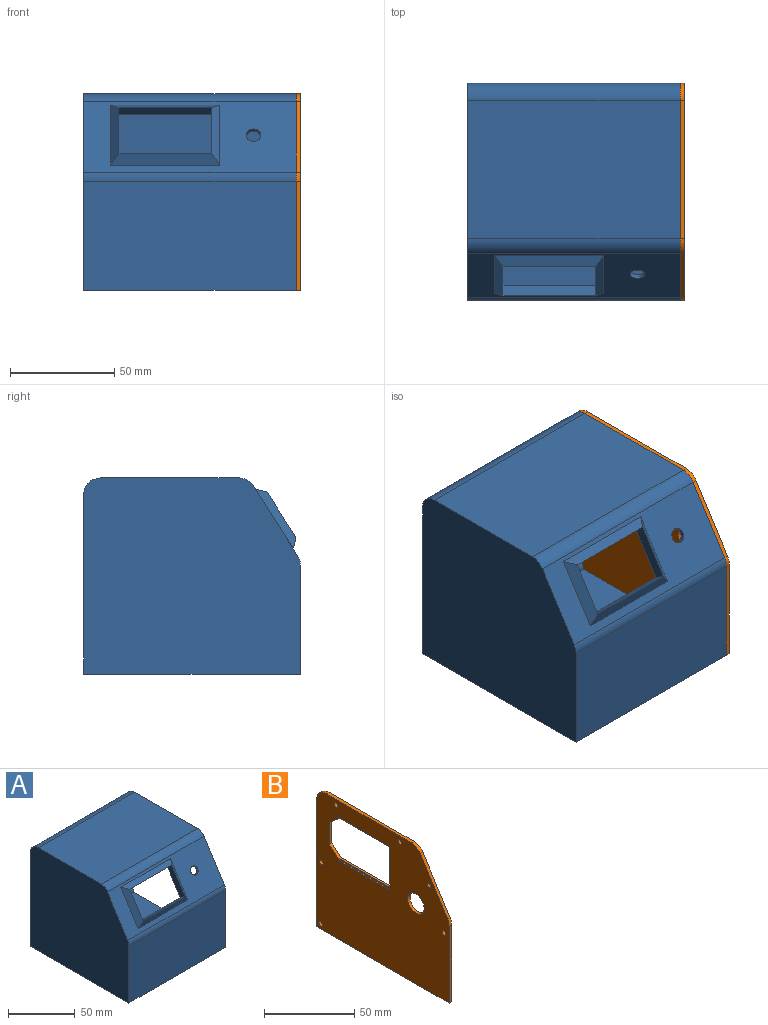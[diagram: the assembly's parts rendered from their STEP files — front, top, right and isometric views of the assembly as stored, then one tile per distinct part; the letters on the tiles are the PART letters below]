
ASSEMBLY  parts=2 mates=1
PART A: 61 faces, bbox 102x104x94 mm
  f0: plane 102x33.74mm, normal (0,-0.84,0.54), area 2255.6mm2, adj f6,f8,f13,f21,f22,f57,f58,f59
  f1: plane 100x49.68mm, normal (0,1,0), area 4888mm2, adj f2,f6,f12,f19,f34,f35,f41,f54
  f2: plane 100x100mm, normal (0,0,1), area 9959.9mm2, adj f1,f6,f11,f12,f32,f33,f38,f54
  f3: plane 100x63.5mm, normal (0,0,-1), area 6204.9mm2, adj f6,f12,f18,f20,f26,f27,f28,f29
  f4: plane 100x32.32mm, normal (0,0.84,-0.54), area 2562.5mm2, adj f6,f12,f13,f14,f15,f16,f17,f19
  f5: plane 102x52.26mm, normal (0,-1,0), area 5330.3mm2, adj f6,f8,f10,f22
  f6: plane 104x94mm, normal (1,0,0), area 931mm2, adj f0,f1,f2,f3,f4,f5,f7,f9
  f7: plane 102x86mm, normal (0,1,0), area 8772mm2, adj f6,f8,f10,f23
  f8: plane 104x94mm, normal (-1,0,0), area 9265.9mm2, adj f0,f5,f7,f9,f10,f21,f22,f23
  f9: plane 102x66.6mm, normal (0,0,1), area 6792.9mm2, adj f6,f8,f21,f23
  f10: plane 104x102mm, normal (0,0,-1), area 10608mm2, adj f5,f6,f7,f8
  f11: plane 100x82mm, normal (0,-1,0), area 8094.8mm2, adj f2,f6,f12,f18,f30,f31,f32,f33
  f12: plane 100x90mm, normal (1,0,0), area 8524.8mm2, adj f1,f2,f3,f4,f11,f18,f19,f20
  f13: cylinder r=3.5mm len=7mm, axis (0,-0.84,0.54), area 44mm2, adj f0,f4
  f14: plane 44.4x5.07mm, normal (0,-0.54,-0.84), area 266.4mm2, adj f4,f15,f17,f58
  f15: plane 25.17x18.99mm, normal (1,0,0), area 156mm2, adj f4,f14,f16,f59
  f16: plane 44.4x5.07mm, normal (0,0.54,0.84), area 266.4mm2, adj f4,f15,f17,f60
  f17: plane 25.17x18.99mm, normal (-1,0,0), area 156mm2, adj f4,f14,f16,f57
  f18: cylinder r=8mm len=100mm, axis (-1,0,0), area 1256.6mm2, adj f3,f6,f11,f12,f28
  f19: cylinder r=8mm len=100mm, axis (-1,0,0), area 452.2mm2, adj f1,f4,f6,f12
  f20: cylinder r=8mm len=100mm, axis (-1,0,0), area 804.4mm2, adj f3,f4,f6,f12
  f21: cylinder r=8mm len=102mm, axis (1,0,0), area 820.5mm2, adj f0,f6,f8,f9
  f22: cylinder r=8mm len=102mm, axis (1,0,0), area 461.3mm2, adj f0,f5,f6,f8
  f23: cylinder r=8mm len=102mm, axis (1,0,0), area 1281.8mm2, adj f6,f7,f8,f9
  f24: cylinder r=5.5mm len=10.14mm, axis (1,0,0), area 86.4mm2, adj f4,f6,f40
  f25: plane 0.56x0.47mm, normal (-1,0,0), area 0.1mm2, adj f4,f40
  f26: cylinder r=5.5mm len=11mm, axis (1,0,0), area 86.4mm2, adj f3,f6,f39
  f27: plane 0.61x0.3mm, normal (-1,0,0), area 0.1mm2, adj f3,f39
  f28: cylinder r=5.5mm len=11mm, axis (1,0,0), area 86.4mm2, adj f3,f6,f18,f36
  f29: plane 0.61x0.3mm, normal (-1,0,0), area 0.1mm2, adj f3,f36
  f30: cylinder r=5.5mm len=11mm, axis (1,0,0), area 86.4mm2, adj f6,f11,f37
  f31: plane 0.61x0.3mm, normal (-1,0,0), area 0.1mm2, adj f11,f37
  f32: cylinder r=5mm len=5mm, axis (1,0,0), area 39.3mm2, adj f2,f6,f11,f38
  f33: plane 0.2x0.2mm, normal (-1,0,0), area 0mm2, adj f2,f11,f38
  f34: cylinder r=5.5mm len=11mm, axis (1,0,0), area 86.4mm2, adj f1,f6,f41
  f35: plane 0.61x0.3mm, normal (-1,0,0), area 0.1mm2, adj f1,f41
  f36: cone r=0.3mm half-angle=60deg, axis (1,0,0), area 54.7mm2, adj f3,f28,f29
  f37: cone r=0.3mm half-angle=60deg, axis (1,0,0), area 54.7mm2, adj f11,f30,f31
  f38: cone r=0.2mm half-angle=58deg, axis (1,0,0), area 23.1mm2, adj f2,f11,f32,f33
  f39: cone r=5.5mm half-angle=60deg, axis (1,0,0), area 54.7mm2, adj f3,f26,f27
  f40: cone r=5.5mm half-angle=60deg, axis (1,0,0), area 54.7mm2, adj f4,f24,f25
  f41: cone r=5.5mm half-angle=60deg, axis (1,0,0), area 54.7mm2, adj f1,f34,f35
  f42: cylinder r=2mm len=5mm, axis (1,0,0), area 62.8mm2, adj f6,f43
  f43: plane 4x4mm, normal (1,0,0), area 12.6mm2, adj f42
  f44: cylinder r=2mm len=5mm, axis (1,0,0), area 62.8mm2, adj f6,f45
  f45: plane 4x4mm, normal (1,0,0), area 12.6mm2, adj f44
  f46: cylinder r=2mm len=5mm, axis (1,0,0), area 62.8mm2, adj f6,f47
  f47: plane 4x4mm, normal (1,0,0), area 12.6mm2, adj f46
  f48: cylinder r=2mm len=5mm, axis (1,0,0), area 62.8mm2, adj f6,f49
  f49: plane 4x4mm, normal (1,0,0), area 12.6mm2, adj f48
  f50: cylinder r=2mm len=5mm, axis (1,0,0), area 62.8mm2, adj f6,f51
  f51: plane 4x4mm, normal (1,0,0), area 12.6mm2, adj f50
  f52: cylinder r=2mm len=5mm, axis (1,0,0), area 62.8mm2, adj f6,f53
  f53: plane 4x4mm, normal (1,0,0), area 12.6mm2, adj f52
  f54: plane 4x4mm, normal (0,0.71,0.71), area 5.7mm2, adj f1,f2,f6,f56
  f55: plane 2.59x2.59mm, normal (-1,0,0), area 3.3mm2, adj f1,f2,f56
  f56: plane 4x4mm, normal (-0.71,0.5,0.5), area 6.6mm2, adj f1,f2,f54,f55
  f57: plane 28.71x19.45mm, normal (0.71,-0.6,0.38), area 169.7mm2, adj f0,f17,f58,f60
  f58: plane 52.4x5.52mm, normal (0,-0.22,0.98), area 273.8mm2, adj f0,f14,f57,f59
  f59: plane 28.71x19.45mm, normal (-0.71,-0.6,0.38), area 169.7mm2, adj f0,f15,f58,f60
  f60: plane 52.4x5.52mm, normal (0,-0.98,-0.22), area 273.8mm2, adj f0,f16,f57,f59
PART B: 29 faces, bbox 2x104x94 mm
  f0: plane 104x94mm, normal (-1,0,0), area 7751.4mm2, adj f2,f3,f4,f5,f6,f7,f8,f9
  f1: plane 104x94mm, normal (1,0,0), area 7831.4mm2, adj f2,f3,f4,f5,f6,f7,f8,f9
  f2: cylinder r=8mm len=8mm, axis (-1,0,0), area 25.1mm2, adj f0,f1,f3,f9
  f3: plane 66.6x2mm, normal (0,0,1), area 133.2mm2, adj f0,f1,f2,f4
  f4: cylinder r=8mm len=6.76mm, axis (-1,0,0), area 16.1mm2, adj f0,f1,f3,f5
  f5: plane 33.74x21.4mm, normal (0,-0.84,0.54), area 79.9mm2, adj f0,f1,f4,f6
  f6: cylinder r=8mm len=4.29mm, axis (-1,0,0), area 9mm2, adj f0,f1,f5,f7
  f7: plane 52.26x2mm, normal (0,-1,0), area 104.5mm2, adj f0,f1,f6,f8
  f8: plane 104x2mm, normal (0,0,-1), area 208mm2, adj f0,f1,f7,f9
  f9: plane 86x2mm, normal (0,1,0), area 172mm2, adj f0,f1,f2,f8
  f10: cylinder r=1.5mm len=3mm, axis (1,0,0), area 18.8mm2, adj f0,f1
  f11: cylinder r=1.5mm len=3mm, axis (1,0,0), area 18.8mm2, adj f0,f1
  f12: cylinder r=1.5mm len=3mm, axis (1,0,0), area 18.8mm2, adj f0,f1
  f13: cylinder r=1.5mm len=3mm, axis (1,0,0), area 18.8mm2, adj f0,f1
  f14: cylinder r=1.5mm len=3mm, axis (1,0,0), area 18.8mm2, adj f0,f1
  f15: cylinder r=1.5mm len=3mm, axis (1,0,0), area 18.8mm2, adj f0,f1
  f16: plane 29.5x2mm, normal (0,1,0), area 56.6mm2, adj f0,f1,f17,f19,f24,f25,f26,f28
  f17: plane 40x1.2mm, normal (0,0,1), area 48mm2, adj f1,f16,f18,f26
  f18: plane 7.5x6.25mm, normal (0,-0.64,0.77), area 19.5mm2, adj f0,f1,f17,f20,f27
  f19: plane 40x1.2mm, normal (0,0,-1), area 48mm2, adj f1,f16,f21,f24
  f20: plane 15x2mm, normal (0,-1,0), area 30mm2, adj f0,f1,f18,f21
  f21: plane 7.5x6.25mm, normal (0,-0.64,-0.77), area 19.5mm2, adj f0,f1,f19,f20,f23
  f22: cylinder r=6.5mm len=13mm, axis (1,0,0), area 81.7mm2, adj f0,f1
  f23: plane 1x0.8mm, normal (0,-1,0), area 0.8mm2, adj f0,f21,f24,f25
  f24: plane 40x1mm, normal (-1,0,0), area 40mm2, adj f16,f19,f23,f25
  f25: plane 40x0.8mm, normal (0,0,-1), area 32mm2, adj f0,f16,f23,f24
  f26: plane 40x1mm, normal (-1,0,0), area 40mm2, adj f16,f17,f27,f28
  f27: plane 1x0.8mm, normal (0,-1,0), area 0.8mm2, adj f0,f18,f26,f28
  f28: plane 40x0.8mm, normal (0,0,1), area 32mm2, adj f0,f16,f26,f27
PLACE A t=(-43.7,-9.14,-21.33)mm fixed
PLACE B t=(-43.7,-9.14,-21.33)mm
MATE slider A.f50 <-> B.f10  axis (1,0,0) through (6.3,-22.53,66.67)mm
